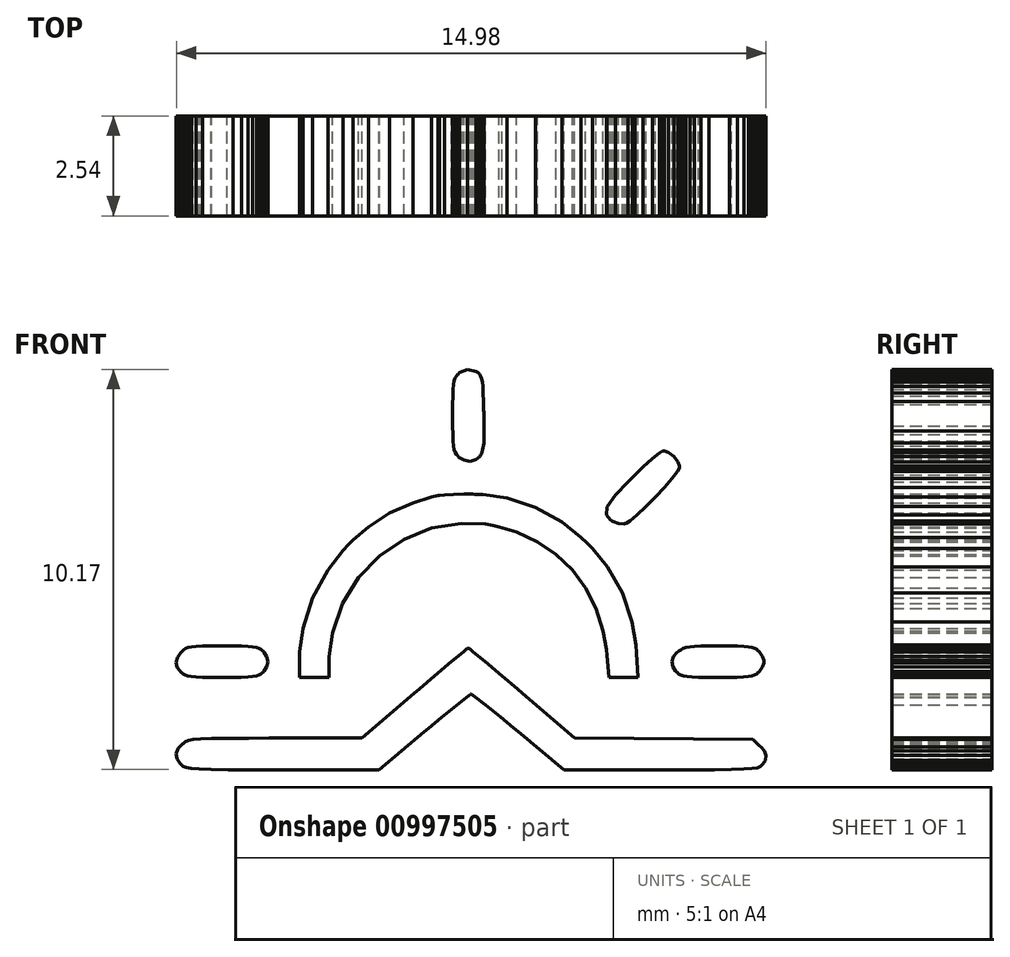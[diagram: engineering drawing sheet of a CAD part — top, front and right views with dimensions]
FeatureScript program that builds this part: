
annotation { "Feature Type Name" : "Feature", "Feature Type Description" : "" }
export const myFeature = defineFeature(function(context is Context, id is Id, definition is map)
    precondition{}
    {
        {
            var Q0;
            Q0=qCreatedBy(makeId("Front.planeOp"),FACE);
            var sketch = newSketch(context, id + "F0", { "sketchPlane" : qUnion([Q0])});
            skLineSegment(sketch, "E0", {"start": v(10.8, 42.86) * mm, "end": v(-8.25, 61.91) * mm});
            skLineSegment(sketch, "E1", {"start": v(-8.26, 61.91) * mm, "end": v(-10.8, 61.91) * mm});
            skLineSegment(sketch, "E2", {"start": v(-10.8, 61.91) * mm, "end": v(-10.8, -61.91) * mm});
            skLineSegment(sketch, "E3", {"start": v(-8.26, -61.91) * mm, "end": v(-10.8, -61.91) * mm});
            skLineSegment(sketch, "E4", {"start": v(-8.26, -61.91) * mm, "end": v(10.8, -42.86) * mm});
            skLineSegment(sketch, "E5", {"start": v(10.8, 42.86) * mm, "end": v(10.8, -42.86) * mm});
            skSolve(sketch);
        }
        {
            var Q0;
            Q0=makeQuery(id+"F0.imprint","IMPRINT",FACE,{"disambiguationData":[TD([[makeQuery(id+"F0.imprint","IMPRINT",EDGE,{"derivedFrom":sQuery(id+"F0.wireOp",EDGE,"E0")}),1.0]])]});
            var sketch = newSketch(context, id + "F1", { "sketchPlane" : qUnion([Q0])});
            skLineSegment(sketch, "E6", {"start": v(-0.33, 44.58) * mm, "end": v(-0.34, 44.57) * mm});
            skLineSegment(sketch, "E7", {"start": v(-0.34, 44.57) * mm, "end": v(-0.37, 44.54) * mm});
            skLineSegment(sketch, "E8", {"start": v(-0.37, 44.54) * mm, "end": v(-0.4, 44.49) * mm});
            skLineSegment(sketch, "E9", {"start": v(-0.4, 44.49) * mm, "end": v(-0.43, 44.42) * mm});
            skLineSegment(sketch, "E10", {"start": v(-0.43, 44.42) * mm, "end": v(-0.45, 44.33) * mm});
            skLineSegment(sketch, "E11", {"start": v(-0.45, 44.33) * mm, "end": v(-0.46, 44.2) * mm});
            skLineSegment(sketch, "E12", {"start": v(-0.46, 44.2) * mm, "end": v(-0.46, 44.04) * mm});
            skLineSegment(sketch, "E13", {"start": v(-0.46, 44.04) * mm, "end": v(-0.47, 43.82) * mm});
            skLineSegment(sketch, "E14", {"start": v(-0.47, 43.82) * mm, "end": v(-0.47, 43.61) * mm});
            skLineSegment(sketch, "E15", {"start": v(-0.47, 43.61) * mm, "end": v(-0.47, 43.55) * mm});
            skLineSegment(sketch, "E16", {"start": v(-0.47, 43.55) * mm, "end": v(-0.47, 43.48) * mm});
            skLineSegment(sketch, "E17", {"start": v(-0.47, 43.48) * mm, "end": v(-0.47, 43.27) * mm});
            skLineSegment(sketch, "E18", {"start": v(-0.47, 43.27) * mm, "end": v(-0.46, 43.06) * mm});
            skLineSegment(sketch, "E19", {"start": v(-0.46, 43.06) * mm, "end": v(-0.46, 42.89) * mm});
            skLineSegment(sketch, "E20", {"start": v(-0.46, 42.89) * mm, "end": v(-0.45, 42.77) * mm});
            skLineSegment(sketch, "E21", {"start": v(-0.45, 42.77) * mm, "end": v(-0.43, 42.67) * mm});
            skLineSegment(sketch, "E22", {"start": v(-0.43, 42.67) * mm, "end": v(-0.4, 42.6) * mm});
            skLineSegment(sketch, "E23", {"start": v(-0.4, 42.6) * mm, "end": v(-0.37, 42.55) * mm});
            skLineSegment(sketch, "E24", {"start": v(-0.37, 42.55) * mm, "end": v(-0.35, 42.52) * mm});
            skLineSegment(sketch, "E25", {"start": v(-0.35, 42.52) * mm, "end": v(-0.33, 42.5) * mm});
            skLineSegment(sketch, "E26", {"start": v(-0.33, 42.5) * mm, "end": v(-0.3, 42.48) * mm});
            skLineSegment(sketch, "E27", {"start": v(-0.3, 42.48) * mm, "end": v(-0.18, 42.4) * mm});
            skLineSegment(sketch, "E28", {"start": v(-0.18, 42.4) * mm, "end": v(-0.03, 42.37) * mm});
            skLineSegment(sketch, "E29", {"start": v(-0.03, 42.37) * mm, "end": v(0.12, 42.42) * mm});
            skLineSegment(sketch, "E30", {"start": v(0.12, 42.42) * mm, "end": v(0.22, 42.5) * mm});
            skLineSegment(sketch, "E31", {"start": v(0.22, 42.5) * mm, "end": v(0.24, 42.53) * mm});
            skLineSegment(sketch, "E32", {"start": v(0.24, 42.53) * mm, "end": v(0.26, 42.56) * mm});
            skLineSegment(sketch, "E33", {"start": v(0.26, 42.56) * mm, "end": v(0.3, 42.66) * mm});
            skLineSegment(sketch, "E34", {"start": v(0.3, 42.66) * mm, "end": v(0.32, 42.84) * mm});
            skLineSegment(sketch, "E35", {"start": v(0.32, 42.84) * mm, "end": v(0.33, 43.15) * mm});
            skLineSegment(sketch, "E36", {"start": v(0.33, 43.15) * mm, "end": v(0.33, 43.5) * mm});
            skLineSegment(sketch, "E37", {"start": v(0.33, 43.5) * mm, "end": v(0.32, 43.61) * mm});
            skLineSegment(sketch, "E38", {"start": v(0.32, 43.61) * mm, "end": v(0.32, 43.68) * mm});
            skLineSegment(sketch, "E39", {"start": v(0.32, 43.68) * mm, "end": v(0.31, 43.89) * mm});
            skLineSegment(sketch, "E40", {"start": v(0.31, 43.89) * mm, "end": v(0.3, 44.1) * mm});
            skLineSegment(sketch, "E41", {"start": v(0.3, 44.1) * mm, "end": v(0.3, 44.27) * mm});
            skLineSegment(sketch, "E42", {"start": v(0.3, 44.27) * mm, "end": v(0.28, 44.4) * mm});
            skLineSegment(sketch, "E43", {"start": v(0.28, 44.4) * mm, "end": v(0.27, 44.48) * mm});
            skLineSegment(sketch, "E44", {"start": v(0.27, 44.48) * mm, "end": v(0.24, 44.54) * mm});
            skLineSegment(sketch, "E45", {"start": v(0.24, 44.54) * mm, "end": v(0.21, 44.59) * mm});
            skLineSegment(sketch, "E46", {"start": v(0.21, 44.59) * mm, "end": v(0.18, 44.62) * mm});
            skLineSegment(sketch, "E47", {"start": v(0.18, 44.62) * mm, "end": v(0.17, 44.62) * mm});
            skLineSegment(sketch, "E48", {"start": v(0.17, 44.62) * mm, "end": v(0.13, 44.66) * mm});
            skLineSegment(sketch, "E49", {"start": v(0.13, 44.66) * mm, "end": v(-0.09, 44.71) * mm});
            skLineSegment(sketch, "E50", {"start": v(-0.09, 44.71) * mm, "end": v(-0.3, 44.62) * mm});
            skLineSegment(sketch, "E51", {"start": v(-0.3, 44.62) * mm, "end": v(-0.33, 44.58) * mm});
            skLineSegment(sketch, "E52", {"start": v(-5.3, 42.5) * mm, "end": v(-5.3, 42.49) * mm});
            skLineSegment(sketch, "E53", {"start": v(-5.3, 42.49) * mm, "end": v(-5.39, 42.37) * mm});
            skLineSegment(sketch, "E54", {"start": v(-5.39, 42.37) * mm, "end": v(-5.43, 42.26) * mm});
            skLineSegment(sketch, "E55", {"start": v(-5.43, 42.26) * mm, "end": v(-5.43, 42.23) * mm});
            skLineSegment(sketch, "E56", {"start": v(-5.43, 42.23) * mm, "end": v(-5.43, 42.2) * mm});
            skLineSegment(sketch, "E57", {"start": v(-5.43, 42.2) * mm, "end": v(-5.37, 42.1) * mm});
            skLineSegment(sketch, "E58", {"start": v(-5.37, 42.1) * mm, "end": v(-5.23, 41.91) * mm});
            skLineSegment(sketch, "E59", {"start": v(-5.23, 41.91) * mm, "end": v(-5.02, 41.68) * mm});
            skLineSegment(sketch, "E60", {"start": v(-5.02, 41.68) * mm, "end": v(-4.77, 41.42) * mm});
            skLineSegment(sketch, "E61", {"start": v(-4.77, 41.42) * mm, "end": v(-4.52, 41.17) * mm});
            skLineSegment(sketch, "E62", {"start": v(-4.52, 41.17) * mm, "end": v(-4.28, 40.97) * mm});
            skLineSegment(sketch, "E63", {"start": v(-4.28, 40.97) * mm, "end": v(-4.09, 40.82) * mm});
            skLineSegment(sketch, "E64", {"start": v(-4.09, 40.82) * mm, "end": v(-4, 40.77) * mm});
            skLineSegment(sketch, "E65", {"start": v(-4, 40.77) * mm, "end": v(-3.96, 40.77) * mm});
            skLineSegment(sketch, "E66", {"start": v(-3.96, 40.77) * mm, "end": v(-3.93, 40.77) * mm});
            skLineSegment(sketch, "E67", {"start": v(-3.93, 40.77) * mm, "end": v(-3.83, 40.8) * mm});
            skLineSegment(sketch, "E68", {"start": v(-3.83, 40.8) * mm, "end": v(-3.7, 40.9) * mm});
            skLineSegment(sketch, "E69", {"start": v(-3.7, 40.9) * mm, "end": v(-3.6, 41.02) * mm});
            skLineSegment(sketch, "E70", {"start": v(-3.6, 41.02) * mm, "end": v(-3.55, 41.1) * mm});
            skLineSegment(sketch, "E71", {"start": v(-3.55, 41.1) * mm, "end": v(-3.55, 41.14) * mm});
            skLineSegment(sketch, "E72", {"start": v(-3.55, 41.14) * mm, "end": v(-3.55, 41.17) * mm});
            skLineSegment(sketch, "E73", {"start": v(-3.55, 41.17) * mm, "end": v(-3.6, 41.25) * mm});
            skLineSegment(sketch, "E74", {"start": v(-3.6, 41.25) * mm, "end": v(-3.76, 41.44) * mm});
            skLineSegment(sketch, "E75", {"start": v(-3.76, 41.44) * mm, "end": v(-3.98, 41.68) * mm});
            skLineSegment(sketch, "E76", {"start": v(-3.98, 41.68) * mm, "end": v(-4.24, 41.95) * mm});
            skLineSegment(sketch, "E77", {"start": v(-4.24, 41.95) * mm, "end": v(-4.5, 42.2) * mm});
            skLineSegment(sketch, "E78", {"start": v(-4.5, 42.2) * mm, "end": v(-4.74, 42.43) * mm});
            skLineSegment(sketch, "E79", {"start": v(-4.74, 42.43) * mm, "end": v(-4.93, 42.58) * mm});
            skLineSegment(sketch, "E80", {"start": v(-4.93, 42.58) * mm, "end": v(-5, 42.64) * mm});
            skLineSegment(sketch, "E81", {"start": v(-5, 42.64) * mm, "end": v(-5.04, 42.64) * mm});
            skLineSegment(sketch, "E82", {"start": v(-5.04, 42.64) * mm, "end": v(-5.07, 42.64) * mm});
            skLineSegment(sketch, "E83", {"start": v(-5.07, 42.64) * mm, "end": v(-5.16, 42.6) * mm});
            skLineSegment(sketch, "E84", {"start": v(-5.16, 42.6) * mm, "end": v(-5.27, 42.53) * mm});
            skLineSegment(sketch, "E85", {"start": v(-5.27, 42.53) * mm, "end": v(-5.3, 42.5) * mm});
            skLineSegment(sketch, "E86", {"start": v(4.1, 41.96) * mm, "end": v(3.98, 41.85) * mm});
            skLineSegment(sketch, "E87", {"start": v(3.98, 41.85) * mm, "end": v(3.66, 41.51) * mm});
            skLineSegment(sketch, "E88", {"start": v(3.66, 41.51) * mm, "end": v(3.45, 41.21) * mm});
            skLineSegment(sketch, "E89", {"start": v(3.45, 41.21) * mm, "end": v(3.43, 41.01) * mm});
            skLineSegment(sketch, "E90", {"start": v(3.43, 41.01) * mm, "end": v(3.54, 40.89) * mm});
            skLineSegment(sketch, "E91", {"start": v(3.54, 40.89) * mm, "end": v(3.58, 40.86) * mm});
            skLineSegment(sketch, "E92", {"start": v(3.58, 40.86) * mm, "end": v(3.6, 40.84) * mm});
            skLineSegment(sketch, "E93", {"start": v(3.6, 40.84) * mm, "end": v(3.74, 40.8) * mm});
            skLineSegment(sketch, "E94", {"start": v(3.74, 40.8) * mm, "end": v(3.88, 40.79) * mm});
            skLineSegment(sketch, "E95", {"start": v(3.88, 40.79) * mm, "end": v(3.9, 40.8) * mm});
            skLineSegment(sketch, "E96", {"start": v(3.9, 40.8) * mm, "end": v(3.94, 40.8) * mm});
            skLineSegment(sketch, "E97", {"start": v(3.94, 40.8) * mm, "end": v(4.03, 40.86) * mm});
            skLineSegment(sketch, "E98", {"start": v(4.03, 40.86) * mm, "end": v(4.22, 41.01) * mm});
            skLineSegment(sketch, "E99", {"start": v(4.22, 41.01) * mm, "end": v(4.44, 41.22) * mm});
            skLineSegment(sketch, "E100", {"start": v(4.44, 41.22) * mm, "end": v(4.68, 41.46) * mm});
            skLineSegment(sketch, "E101", {"start": v(4.68, 41.46) * mm, "end": v(4.91, 41.7) * mm});
            skLineSegment(sketch, "E102", {"start": v(4.91, 41.7) * mm, "end": v(5.1, 41.94) * mm});
            skLineSegment(sketch, "E103", {"start": v(5.1, 41.94) * mm, "end": v(5.24, 42.12) * mm});
            skLineSegment(sketch, "E104", {"start": v(5.24, 42.12) * mm, "end": v(5.3, 42.2) * mm});
            skLineSegment(sketch, "E105", {"start": v(5.3, 42.2) * mm, "end": v(5.3, 42.23) * mm});
            skLineSegment(sketch, "E106", {"start": v(5.3, 42.23) * mm, "end": v(5.3, 42.26) * mm});
            skLineSegment(sketch, "E107", {"start": v(5.3, 42.26) * mm, "end": v(5.25, 42.36) * mm});
            skLineSegment(sketch, "E108", {"start": v(5.25, 42.36) * mm, "end": v(5.15, 42.5) * mm});
            skLineSegment(sketch, "E109", {"start": v(5.15, 42.5) * mm, "end": v(5.02, 42.6) * mm});
            skLineSegment(sketch, "E110", {"start": v(5.02, 42.6) * mm, "end": v(4.92, 42.64) * mm});
            skLineSegment(sketch, "E111", {"start": v(4.92, 42.64) * mm, "end": v(4.88, 42.64) * mm});
            skLineSegment(sketch, "E112", {"start": v(4.88, 42.64) * mm, "end": v(4.86, 42.64) * mm});
            skLineSegment(sketch, "E113", {"start": v(4.86, 42.64) * mm, "end": v(4.78, 42.59) * mm});
            skLineSegment(sketch, "E114", {"start": v(4.78, 42.59) * mm, "end": v(4.6, 42.44) * mm});
            skLineSegment(sketch, "E115", {"start": v(4.6, 42.44) * mm, "end": v(4.36, 42.23) * mm});
            skLineSegment(sketch, "E116", {"start": v(4.36, 42.23) * mm, "end": v(4.16, 42.03) * mm});
            skLineSegment(sketch, "E117", {"start": v(4.16, 42.03) * mm, "end": v(4.1, 41.96) * mm});
            skLineSegment(sketch, "E118", {"start": v(-0.84, 41.5) * mm, "end": v(-1, 41.47) * mm});
            skLineSegment(sketch, "E119", {"start": v(-1, 41.47) * mm, "end": v(-1.48, 41.32) * mm});
            skLineSegment(sketch, "E120", {"start": v(-1.48, 41.32) * mm, "end": v(-2.07, 41.06) * mm});
            skLineSegment(sketch, "E121", {"start": v(-2.07, 41.06) * mm, "end": v(-2.6, 40.7) * mm});
            skLineSegment(sketch, "E122", {"start": v(-2.6, 40.7) * mm, "end": v(-3, 40.38) * mm});
            skLineSegment(sketch, "E123", {"start": v(-3, 40.38) * mm, "end": v(-3.11, 40.26) * mm});
            skLineSegment(sketch, "E124", {"start": v(-3.11, 40.26) * mm, "end": v(-3.26, 40.11) * mm});
            skLineSegment(sketch, "E125", {"start": v(-3.26, 40.11) * mm, "end": v(-3.64, 39.62) * mm});
            skLineSegment(sketch, "E126", {"start": v(-3.64, 39.62) * mm, "end": v(-4.03, 38.9) * mm});
            skLineSegment(sketch, "E127", {"start": v(-4.03, 38.9) * mm, "end": v(-4.27, 38.13) * mm});
            skLineSegment(sketch, "E128", {"start": v(-4.27, 38.13) * mm, "end": v(-4.35, 37.53) * mm});
            skLineSegment(sketch, "E129", {"start": v(-4.35, 37.53) * mm, "end": v(-4.35, 37.34) * mm});
            skLineSegment(sketch, "E130", {"start": v(-4.35, 37.34) * mm, "end": v(-4.35, 36.88) * mm});
            skLineSegment(sketch, "E131", {"start": v(-4.35, 36.88) * mm, "end": v(-3.62, 36.88) * mm});
            skLineSegment(sketch, "E132", {"start": v(-3.62, 36.88) * mm, "end": v(-3.62, 37.2) * mm});
            skLineSegment(sketch, "E133", {"start": v(-3.62, 37.2) * mm, "end": v(-3.62, 37.4) * mm});
            skLineSegment(sketch, "E134", {"start": v(-3.62, 37.4) * mm, "end": v(-3.52, 38.02) * mm});
            skLineSegment(sketch, "E135", {"start": v(-3.52, 38.02) * mm, "end": v(-3.26, 38.76) * mm});
            skLineSegment(sketch, "E136", {"start": v(-3.26, 38.76) * mm, "end": v(-2.86, 39.42) * mm});
            skLineSegment(sketch, "E137", {"start": v(-2.86, 39.42) * mm, "end": v(-2.33, 39.97) * mm});
            skLineSegment(sketch, "E138", {"start": v(-2.33, 39.97) * mm, "end": v(-1.7, 40.4) * mm});
            skLineSegment(sketch, "E139", {"start": v(-1.7, 40.4) * mm, "end": v(-1, 40.68) * mm});
            skLineSegment(sketch, "E140", {"start": v(-1, 40.68) * mm, "end": v(-0.24, 40.8) * mm});
            skLineSegment(sketch, "E141", {"start": v(-0.24, 40.8) * mm, "end": v(0.36, 40.78) * mm});
            skLineSegment(sketch, "E142", {"start": v(0.36, 40.78) * mm, "end": v(0.56, 40.74) * mm});
            skLineSegment(sketch, "E143", {"start": v(0.56, 40.74) * mm, "end": v(0.7, 40.7) * mm});
            skLineSegment(sketch, "E144", {"start": v(0.7, 40.7) * mm, "end": v(1.15, 40.58) * mm});
            skLineSegment(sketch, "E145", {"start": v(1.15, 40.58) * mm, "end": v(1.68, 40.33) * mm});
            skLineSegment(sketch, "E146", {"start": v(1.68, 40.33) * mm, "end": v(2.16, 40) * mm});
            skLineSegment(sketch, "E147", {"start": v(2.16, 40) * mm, "end": v(2.57, 39.61) * mm});
            skLineSegment(sketch, "E148", {"start": v(2.57, 39.61) * mm, "end": v(2.9, 39.15) * mm});
            skLineSegment(sketch, "E149", {"start": v(2.9, 39.15) * mm, "end": v(3.17, 38.63) * mm});
            skLineSegment(sketch, "E150", {"start": v(3.17, 38.63) * mm, "end": v(3.35, 38.06) * mm});
            skLineSegment(sketch, "E151", {"start": v(3.35, 38.06) * mm, "end": v(3.44, 37.6) * mm});
            skLineSegment(sketch, "E152", {"start": v(3.44, 37.6) * mm, "end": v(3.45, 37.44) * mm});
            skLineSegment(sketch, "E153", {"start": v(3.45, 37.44) * mm, "end": v(3.5, 36.88) * mm});
            skLineSegment(sketch, "E154", {"start": v(3.5, 36.88) * mm, "end": v(4.24, 36.88) * mm});
            skLineSegment(sketch, "E155", {"start": v(4.24, 36.88) * mm, "end": v(4.2, 37.5) * mm});
            skLineSegment(sketch, "E156", {"start": v(4.2, 37.5) * mm, "end": v(4.19, 37.7) * mm});
            skLineSegment(sketch, "E157", {"start": v(4.19, 37.7) * mm, "end": v(4.09, 38.3) * mm});
            skLineSegment(sketch, "E158", {"start": v(4.09, 38.3) * mm, "end": v(3.84, 39.02) * mm});
            skLineSegment(sketch, "E159", {"start": v(3.84, 39.02) * mm, "end": v(3.46, 39.69) * mm});
            skLineSegment(sketch, "E160", {"start": v(3.46, 39.69) * mm, "end": v(3.08, 40.16) * mm});
            skLineSegment(sketch, "E161", {"start": v(3.08, 40.16) * mm, "end": v(2.94, 40.3) * mm});
            skLineSegment(sketch, "E162", {"start": v(2.94, 40.3) * mm, "end": v(2.8, 40.44) * mm});
            skLineSegment(sketch, "E163", {"start": v(2.8, 40.44) * mm, "end": v(2.3, 40.83) * mm});
            skLineSegment(sketch, "E164", {"start": v(2.3, 40.83) * mm, "end": v(1.64, 41.2) * mm});
            skLineSegment(sketch, "E165", {"start": v(1.64, 41.2) * mm, "end": v(0.9, 41.44) * mm});
            skLineSegment(sketch, "E166", {"start": v(0.9, 41.44) * mm, "end": v(0.3, 41.53) * mm});
            skLineSegment(sketch, "E167", {"start": v(0.3, 41.53) * mm, "end": v(0.1, 41.54) * mm});
            skLineSegment(sketch, "E168", {"start": v(0.1, 41.54) * mm, "end": v(0.03, 41.54) * mm});
            skLineSegment(sketch, "E169", {"start": v(0.03, 41.54) * mm, "end": v(-0.18, 41.54) * mm});
            skLineSegment(sketch, "E170", {"start": v(-0.18, 41.54) * mm, "end": v(-0.45, 41.54) * mm});
            skLineSegment(sketch, "E171", {"start": v(-0.45, 41.54) * mm, "end": v(-0.68, 41.52) * mm});
            skLineSegment(sketch, "E172", {"start": v(-0.68, 41.52) * mm, "end": v(-0.8, 41.51) * mm});
            skLineSegment(sketch, "E173", {"start": v(-0.8, 41.51) * mm, "end": v(-0.84, 41.5) * mm});
            skLineSegment(sketch, "E174", {"start": v(-7.35, 37.53) * mm, "end": v(-7.38, 37.5) * mm});
            skLineSegment(sketch, "E175", {"start": v(-7.38, 37.5) * mm, "end": v(-7.46, 37.4) * mm});
            skLineSegment(sketch, "E176", {"start": v(-7.46, 37.4) * mm, "end": v(-7.5, 37.26) * mm});
            skLineSegment(sketch, "E177", {"start": v(-7.5, 37.26) * mm, "end": v(-7.46, 37.14) * mm});
            skLineSegment(sketch, "E178", {"start": v(-7.46, 37.14) * mm, "end": v(-7.4, 37.04) * mm});
            skLineSegment(sketch, "E179", {"start": v(-7.4, 37.04) * mm, "end": v(-7.37, 37.01) * mm});
            skLineSegment(sketch, "E180", {"start": v(-7.37, 37.01) * mm, "end": v(-7.36, 37) * mm});
            skLineSegment(sketch, "E181", {"start": v(-7.36, 37) * mm, "end": v(-7.32, 36.97) * mm});
            skLineSegment(sketch, "E182", {"start": v(-7.32, 36.97) * mm, "end": v(-7.27, 36.94) * mm});
            skLineSegment(sketch, "E183", {"start": v(-7.27, 36.94) * mm, "end": v(-7.2, 36.92) * mm});
            skLineSegment(sketch, "E184", {"start": v(-7.2, 36.92) * mm, "end": v(-7.1, 36.9) * mm});
            skLineSegment(sketch, "E185", {"start": v(-7.1, 36.9) * mm, "end": v(-6.99, 36.9) * mm});
            skLineSegment(sketch, "E186", {"start": v(-6.99, 36.9) * mm, "end": v(-6.82, 36.88) * mm});
            skLineSegment(sketch, "E187", {"start": v(-6.82, 36.88) * mm, "end": v(-6.6, 36.88) * mm});
            skLineSegment(sketch, "E188", {"start": v(-6.6, 36.88) * mm, "end": v(-6.4, 36.88) * mm});
            skLineSegment(sketch, "E189", {"start": v(-6.4, 36.88) * mm, "end": v(-6.33, 36.88) * mm});
            skLineSegment(sketch, "E190", {"start": v(-6.33, 36.88) * mm, "end": v(-6.26, 36.88) * mm});
            skLineSegment(sketch, "E191", {"start": v(-6.26, 36.88) * mm, "end": v(-6.06, 36.88) * mm});
            skLineSegment(sketch, "E192", {"start": v(-6.06, 36.88) * mm, "end": v(-5.84, 36.88) * mm});
            skLineSegment(sketch, "E193", {"start": v(-5.84, 36.88) * mm, "end": v(-5.67, 36.9) * mm});
            skLineSegment(sketch, "E194", {"start": v(-5.67, 36.9) * mm, "end": v(-5.55, 36.9) * mm});
            skLineSegment(sketch, "E195", {"start": v(-5.55, 36.9) * mm, "end": v(-5.46, 36.92) * mm});
            skLineSegment(sketch, "E196", {"start": v(-5.46, 36.92) * mm, "end": v(-5.39, 36.94) * mm});
            skLineSegment(sketch, "E197", {"start": v(-5.39, 36.94) * mm, "end": v(-5.34, 36.97) * mm});
            skLineSegment(sketch, "E198", {"start": v(-5.34, 36.97) * mm, "end": v(-5.3, 37) * mm});
            skLineSegment(sketch, "E199", {"start": v(-5.3, 37) * mm, "end": v(-5.3, 37.01) * mm});
            skLineSegment(sketch, "E200", {"start": v(-5.3, 37.01) * mm, "end": v(-5.26, 37.04) * mm});
            skLineSegment(sketch, "E201", {"start": v(-5.26, 37.04) * mm, "end": v(-5.2, 37.15) * mm});
            skLineSegment(sketch, "E202", {"start": v(-5.2, 37.15) * mm, "end": v(-5.17, 37.28) * mm});
            skLineSegment(sketch, "E203", {"start": v(-5.17, 37.28) * mm, "end": v(-5.2, 37.42) * mm});
            skLineSegment(sketch, "E204", {"start": v(-5.2, 37.42) * mm, "end": v(-5.26, 37.52) * mm});
            skLineSegment(sketch, "E205", {"start": v(-5.26, 37.52) * mm, "end": v(-5.3, 37.55) * mm});
            skLineSegment(sketch, "E206", {"start": v(-5.3, 37.55) * mm, "end": v(-5.3, 37.56) * mm});
            skLineSegment(sketch, "E207", {"start": v(-5.3, 37.56) * mm, "end": v(-5.34, 37.6) * mm});
            skLineSegment(sketch, "E208", {"start": v(-5.34, 37.6) * mm, "end": v(-5.39, 37.62) * mm});
            skLineSegment(sketch, "E209", {"start": v(-5.39, 37.62) * mm, "end": v(-5.46, 37.65) * mm});
            skLineSegment(sketch, "E210", {"start": v(-5.46, 37.65) * mm, "end": v(-5.55, 37.66) * mm});
            skLineSegment(sketch, "E211", {"start": v(-5.55, 37.66) * mm, "end": v(-5.67, 37.67) * mm});
            skLineSegment(sketch, "E212", {"start": v(-5.67, 37.67) * mm, "end": v(-5.83, 37.68) * mm});
            skLineSegment(sketch, "E213", {"start": v(-5.83, 37.68) * mm, "end": v(-6.05, 37.68) * mm});
            skLineSegment(sketch, "E214", {"start": v(-6.05, 37.68) * mm, "end": v(-6.25, 37.68) * mm});
            skLineSegment(sketch, "E215", {"start": v(-6.25, 37.68) * mm, "end": v(-6.32, 37.68) * mm});
            skLineSegment(sketch, "E216", {"start": v(-6.32, 37.68) * mm, "end": v(-6.39, 37.68) * mm});
            skLineSegment(sketch, "E217", {"start": v(-6.39, 37.68) * mm, "end": v(-6.6, 37.68) * mm});
            skLineSegment(sketch, "E218", {"start": v(-6.6, 37.68) * mm, "end": v(-6.82, 37.68) * mm});
            skLineSegment(sketch, "E219", {"start": v(-6.82, 37.68) * mm, "end": v(-6.98, 37.67) * mm});
            skLineSegment(sketch, "E220", {"start": v(-6.98, 37.67) * mm, "end": v(-7.1, 37.66) * mm});
            skLineSegment(sketch, "E221", {"start": v(-7.1, 37.66) * mm, "end": v(-7.2, 37.64) * mm});
            skLineSegment(sketch, "E222", {"start": v(-7.2, 37.64) * mm, "end": v(-7.26, 37.62) * mm});
            skLineSegment(sketch, "E223", {"start": v(-7.26, 37.62) * mm, "end": v(-7.3, 37.58) * mm});
            skLineSegment(sketch, "E224", {"start": v(-7.3, 37.58) * mm, "end": v(-7.34, 37.54) * mm});
            skLineSegment(sketch, "E225", {"start": v(-7.34, 37.54) * mm, "end": v(-7.35, 37.53) * mm});
            skLineSegment(sketch, "E226", {"start": v(5.27, 37.54) * mm, "end": v(5.23, 37.52) * mm});
            skLineSegment(sketch, "E227", {"start": v(5.23, 37.52) * mm, "end": v(5.15, 37.42) * mm});
            skLineSegment(sketch, "E228", {"start": v(5.15, 37.42) * mm, "end": v(5.1, 37.29) * mm});
            skLineSegment(sketch, "E229", {"start": v(5.1, 37.29) * mm, "end": v(5.13, 37.15) * mm});
            skLineSegment(sketch, "E230", {"start": v(5.13, 37.15) * mm, "end": v(5.2, 37.04) * mm});
            skLineSegment(sketch, "E231", {"start": v(5.2, 37.04) * mm, "end": v(5.23, 37.01) * mm});
            skLineSegment(sketch, "E232", {"start": v(5.23, 37.01) * mm, "end": v(5.24, 37) * mm});
            skLineSegment(sketch, "E233", {"start": v(5.24, 37) * mm, "end": v(5.27, 36.97) * mm});
            skLineSegment(sketch, "E234", {"start": v(5.27, 36.97) * mm, "end": v(5.32, 36.94) * mm});
            skLineSegment(sketch, "E235", {"start": v(5.32, 36.94) * mm, "end": v(5.4, 36.92) * mm});
            skLineSegment(sketch, "E236", {"start": v(5.4, 36.92) * mm, "end": v(5.48, 36.9) * mm});
            skLineSegment(sketch, "E237", {"start": v(5.48, 36.9) * mm, "end": v(5.6, 36.9) * mm});
            skLineSegment(sketch, "E238", {"start": v(5.6, 36.9) * mm, "end": v(5.77, 36.88) * mm});
            skLineSegment(sketch, "E239", {"start": v(5.77, 36.88) * mm, "end": v(5.99, 36.88) * mm});
            skLineSegment(sketch, "E240", {"start": v(5.99, 36.88) * mm, "end": v(6.2, 36.88) * mm});
            skLineSegment(sketch, "E241", {"start": v(6.2, 36.88) * mm, "end": v(6.26, 36.88) * mm});
            skLineSegment(sketch, "E242", {"start": v(6.26, 36.88) * mm, "end": v(6.33, 36.88) * mm});
            skLineSegment(sketch, "E243", {"start": v(6.33, 36.88) * mm, "end": v(6.54, 36.88) * mm});
            skLineSegment(sketch, "E244", {"start": v(6.54, 36.88) * mm, "end": v(6.75, 36.88) * mm});
            skLineSegment(sketch, "E245", {"start": v(6.75, 36.88) * mm, "end": v(6.92, 36.9) * mm});
            skLineSegment(sketch, "E246", {"start": v(6.92, 36.9) * mm, "end": v(7.04, 36.9) * mm});
            skLineSegment(sketch, "E247", {"start": v(7.04, 36.9) * mm, "end": v(7.14, 36.92) * mm});
            skLineSegment(sketch, "E248", {"start": v(7.14, 36.92) * mm, "end": v(7.2, 36.94) * mm});
            skLineSegment(sketch, "E249", {"start": v(7.2, 36.94) * mm, "end": v(7.26, 36.97) * mm});
            skLineSegment(sketch, "E250", {"start": v(7.26, 36.97) * mm, "end": v(7.3, 37) * mm});
            skLineSegment(sketch, "E251", {"start": v(7.3, 37) * mm, "end": v(7.3, 37.01) * mm});
            skLineSegment(sketch, "E252", {"start": v(7.3, 37.01) * mm, "end": v(7.32, 37.03) * mm});
            skLineSegment(sketch, "E253", {"start": v(7.32, 37.03) * mm, "end": v(7.4, 37.15) * mm});
            skLineSegment(sketch, "E254", {"start": v(7.4, 37.15) * mm, "end": v(7.44, 37.25) * mm});
            skLineSegment(sketch, "E255", {"start": v(7.44, 37.25) * mm, "end": v(7.44, 37.28) * mm});
            skLineSegment(sketch, "E256", {"start": v(7.44, 37.28) * mm, "end": v(7.44, 37.32) * mm});
            skLineSegment(sketch, "E257", {"start": v(7.44, 37.32) * mm, "end": v(7.4, 37.42) * mm});
            skLineSegment(sketch, "E258", {"start": v(7.4, 37.42) * mm, "end": v(7.32, 37.53) * mm});
            skLineSegment(sketch, "E259", {"start": v(7.32, 37.53) * mm, "end": v(7.3, 37.55) * mm});
            skLineSegment(sketch, "E260", {"start": v(7.3, 37.55) * mm, "end": v(7.3, 37.56) * mm});
            skLineSegment(sketch, "E261", {"start": v(7.3, 37.56) * mm, "end": v(7.26, 37.6) * mm});
            skLineSegment(sketch, "E262", {"start": v(7.26, 37.6) * mm, "end": v(7.2, 37.62) * mm});
            skLineSegment(sketch, "E263", {"start": v(7.2, 37.62) * mm, "end": v(7.14, 37.65) * mm});
            skLineSegment(sketch, "E264", {"start": v(7.14, 37.65) * mm, "end": v(7.05, 37.66) * mm});
            skLineSegment(sketch, "E265", {"start": v(7.05, 37.66) * mm, "end": v(6.93, 37.67) * mm});
            skLineSegment(sketch, "E266", {"start": v(6.93, 37.67) * mm, "end": v(6.77, 37.68) * mm});
            skLineSegment(sketch, "E267", {"start": v(6.77, 37.68) * mm, "end": v(6.56, 37.68) * mm});
            skLineSegment(sketch, "E268", {"start": v(6.56, 37.68) * mm, "end": v(6.37, 37.68) * mm});
            skLineSegment(sketch, "E269", {"start": v(6.37, 37.68) * mm, "end": v(6.3, 37.68) * mm});
            skLineSegment(sketch, "E270", {"start": v(6.3, 37.68) * mm, "end": v(6.24, 37.68) * mm});
            skLineSegment(sketch, "E271", {"start": v(6.24, 37.68) * mm, "end": v(6.04, 37.68) * mm});
            skLineSegment(sketch, "E272", {"start": v(6.04, 37.68) * mm, "end": v(5.84, 37.68) * mm});
            skLineSegment(sketch, "E273", {"start": v(5.84, 37.68) * mm, "end": v(5.68, 37.67) * mm});
            skLineSegment(sketch, "E274", {"start": v(5.68, 37.67) * mm, "end": v(5.56, 37.66) * mm});
            skLineSegment(sketch, "E275", {"start": v(5.56, 37.66) * mm, "end": v(5.46, 37.64) * mm});
            skLineSegment(sketch, "E276", {"start": v(5.46, 37.64) * mm, "end": v(5.39, 37.62) * mm});
            skLineSegment(sketch, "E277", {"start": v(5.39, 37.62) * mm, "end": v(5.32, 37.59) * mm});
            skLineSegment(sketch, "E278", {"start": v(5.32, 37.59) * mm, "end": v(5.28, 37.55) * mm});
            skLineSegment(sketch, "E279", {"start": v(5.28, 37.55) * mm, "end": v(5.27, 37.54) * mm});
            skLineSegment(sketch, "E280", {"start": v(-1.45, 36.48) * mm, "end": v(-2.77, 35.34) * mm});
            skLineSegment(sketch, "E281", {"start": v(-2.77, 35.34) * mm, "end": v(-4.96, 35.34) * mm});
            skLineSegment(sketch, "E282", {"start": v(-4.96, 35.34) * mm, "end": v(-5.13, 35.34) * mm});
            skLineSegment(sketch, "E283", {"start": v(-5.13, 35.34) * mm, "end": v(-5.66, 35.34) * mm});
            skLineSegment(sketch, "E284", {"start": v(-5.66, 35.34) * mm, "end": v(-6.2, 35.34) * mm});
            skLineSegment(sketch, "E285", {"start": v(-6.2, 35.34) * mm, "end": v(-6.6, 35.33) * mm});
            skLineSegment(sketch, "E286", {"start": v(-6.6, 35.33) * mm, "end": v(-6.87, 35.32) * mm});
            skLineSegment(sketch, "E287", {"start": v(-6.87, 35.32) * mm, "end": v(-7.06, 35.3) * mm});
            skLineSegment(sketch, "E288", {"start": v(-7.06, 35.3) * mm, "end": v(-7.18, 35.28) * mm});
            skLineSegment(sketch, "E289", {"start": v(-7.18, 35.28) * mm, "end": v(-7.26, 35.24) * mm});
            skLineSegment(sketch, "E290", {"start": v(-7.26, 35.24) * mm, "end": v(-7.31, 35.21) * mm});
            skLineSegment(sketch, "E291", {"start": v(-7.31, 35.21) * mm, "end": v(-7.33, 35.2) * mm});
            skLineSegment(sketch, "E292", {"start": v(-7.33, 35.2) * mm, "end": v(-7.36, 35.17) * mm});
            skLineSegment(sketch, "E293", {"start": v(-7.36, 35.17) * mm, "end": v(-7.45, 35.07) * mm});
            skLineSegment(sketch, "E294", {"start": v(-7.45, 35.07) * mm, "end": v(-7.5, 34.94) * mm});
            skLineSegment(sketch, "E295", {"start": v(-7.5, 34.94) * mm, "end": v(-7.47, 34.8) * mm});
            skLineSegment(sketch, "E296", {"start": v(-7.47, 34.8) * mm, "end": v(-7.4, 34.7) * mm});
            skLineSegment(sketch, "E297", {"start": v(-7.4, 34.7) * mm, "end": v(-7.37, 34.67) * mm});
            skLineSegment(sketch, "E298", {"start": v(-7.37, 34.67) * mm, "end": v(-7.36, 34.66) * mm});
            skLineSegment(sketch, "E299", {"start": v(-7.36, 34.66) * mm, "end": v(-7.32, 34.63) * mm});
            skLineSegment(sketch, "E300", {"start": v(-7.32, 34.63) * mm, "end": v(-7.24, 34.6) * mm});
            skLineSegment(sketch, "E301", {"start": v(-7.24, 34.6) * mm, "end": v(-7.12, 34.57) * mm});
            skLineSegment(sketch, "E302", {"start": v(-7.12, 34.57) * mm, "end": v(-6.91, 34.56) * mm});
            skLineSegment(sketch, "E303", {"start": v(-6.91, 34.56) * mm, "end": v(-6.6, 34.54) * mm});
            skLineSegment(sketch, "E304", {"start": v(-6.6, 34.54) * mm, "end": v(-6.17, 34.54) * mm});
            skLineSegment(sketch, "E305", {"start": v(-6.17, 34.54) * mm, "end": v(-5.57, 34.54) * mm});
            skLineSegment(sketch, "E306", {"start": v(-5.57, 34.54) * mm, "end": v(-4.98, 34.54) * mm});
            skLineSegment(sketch, "E307", {"start": v(-4.98, 34.54) * mm, "end": v(-4.79, 34.54) * mm});
            skLineSegment(sketch, "E308", {"start": v(-4.79, 34.54) * mm, "end": v(-2.34, 34.54) * mm});
            skLineSegment(sketch, "E309", {"start": v(-2.34, 34.54) * mm, "end": v(-1.2, 35.5) * mm});
            skLineSegment(sketch, "E310", {"start": v(-1.2, 35.5) * mm, "end": v(-1.09, 35.59) * mm});
            skLineSegment(sketch, "E311", {"start": v(-1.09, 35.59) * mm, "end": v(-0.75, 35.86) * mm});
            skLineSegment(sketch, "E312", {"start": v(-0.75, 35.86) * mm, "end": v(-0.38, 36.17) * mm});
            skLineSegment(sketch, "E313", {"start": v(-0.38, 36.17) * mm, "end": v(-0.12, 36.38) * mm});
            skLineSegment(sketch, "E314", {"start": v(-0.12, 36.38) * mm, "end": v(-0.02, 36.46) * mm});
            skLineSegment(sketch, "E315", {"start": v(-0.02, 36.46) * mm, "end": v(-0.01, 36.46) * mm});
            skLineSegment(sketch, "E316", {"start": v(-0.01, 36.46) * mm, "end": v(0, 36.46) * mm});
            skLineSegment(sketch, "E317", {"start": v(0, 36.46) * mm, "end": v(0.1, 36.39) * mm});
            skLineSegment(sketch, "E318", {"start": v(0.1, 36.39) * mm, "end": v(0.36, 36.19) * mm});
            skLineSegment(sketch, "E319", {"start": v(0.36, 36.19) * mm, "end": v(0.74, 35.88) * mm});
            skLineSegment(sketch, "E320", {"start": v(0.74, 35.88) * mm, "end": v(1.08, 35.6) * mm});
            skLineSegment(sketch, "E321", {"start": v(1.08, 35.6) * mm, "end": v(1.2, 35.5) * mm});
            skLineSegment(sketch, "E322", {"start": v(1.2, 35.5) * mm, "end": v(2.36, 34.54) * mm});
            skLineSegment(sketch, "E323", {"start": v(2.36, 34.54) * mm, "end": v(4.82, 34.54) * mm});
            skLineSegment(sketch, "E324", {"start": v(4.82, 34.54) * mm, "end": v(5, 34.54) * mm});
            skLineSegment(sketch, "E325", {"start": v(5, 34.54) * mm, "end": v(5.58, 34.54) * mm});
            skLineSegment(sketch, "E326", {"start": v(5.58, 34.54) * mm, "end": v(6.18, 34.54) * mm});
            skLineSegment(sketch, "E327", {"start": v(6.18, 34.54) * mm, "end": v(6.62, 34.54) * mm});
            skLineSegment(sketch, "E328", {"start": v(6.62, 34.54) * mm, "end": v(6.93, 34.55) * mm});
            skLineSegment(sketch, "E329", {"start": v(6.93, 34.55) * mm, "end": v(7.14, 34.57) * mm});
            skLineSegment(sketch, "E330", {"start": v(7.14, 34.57) * mm, "end": v(7.27, 34.59) * mm});
            skLineSegment(sketch, "E331", {"start": v(7.27, 34.59) * mm, "end": v(7.34, 34.62) * mm});
            skLineSegment(sketch, "E332", {"start": v(7.34, 34.62) * mm, "end": v(7.38, 34.65) * mm});
            skLineSegment(sketch, "E333", {"start": v(7.38, 34.65) * mm, "end": v(7.39, 34.66) * mm});
            skLineSegment(sketch, "E334", {"start": v(7.39, 34.66) * mm, "end": v(7.41, 34.68) * mm});
            skLineSegment(sketch, "E335", {"start": v(7.41, 34.68) * mm, "end": v(7.48, 34.78) * mm});
            skLineSegment(sketch, "E336", {"start": v(7.48, 34.78) * mm, "end": v(7.5, 34.9) * mm});
            skLineSegment(sketch, "E337", {"start": v(7.5, 34.9) * mm, "end": v(7.45, 35.01) * mm});
            skLineSegment(sketch, "E338", {"start": v(7.45, 35.01) * mm, "end": v(7.36, 35.12) * mm});
            skLineSegment(sketch, "E339", {"start": v(7.36, 35.12) * mm, "end": v(7.33, 35.15) * mm});
            skLineSegment(sketch, "E340", {"start": v(7.33, 35.15) * mm, "end": v(7.15, 35.3) * mm});
            skLineSegment(sketch, "E341", {"start": v(7.15, 35.3) * mm, "end": v(2.63, 35.35) * mm});
            skLineSegment(sketch, "E342", {"start": v(2.63, 35.35) * mm, "end": v(1.3, 36.48) * mm});
            skLineSegment(sketch, "E343", {"start": v(1.3, 36.48) * mm, "end": v(1.17, 36.6) * mm});
            skLineSegment(sketch, "E344", {"start": v(1.17, 36.6) * mm, "end": v(0.78, 36.92) * mm});
            skLineSegment(sketch, "E345", {"start": v(0.78, 36.92) * mm, "end": v(0.35, 37.28) * mm});
            skLineSegment(sketch, "E346", {"start": v(0.35, 37.28) * mm, "end": v(0.05, 37.53) * mm});
            skLineSegment(sketch, "E347", {"start": v(0.05, 37.53) * mm, "end": v(-0.04, 37.62) * mm});
            skLineSegment(sketch, "E348", {"start": v(-0.04, 37.62) * mm, "end": v(-0.07, 37.62) * mm});
            skLineSegment(sketch, "E349", {"start": v(-0.07, 37.62) * mm, "end": v(-0.1, 37.62) * mm});
            skLineSegment(sketch, "E350", {"start": v(-0.1, 37.62) * mm, "end": v(-0.2, 37.53) * mm});
            skLineSegment(sketch, "E351", {"start": v(-0.2, 37.53) * mm, "end": v(-0.5, 37.28) * mm});
            skLineSegment(sketch, "E352", {"start": v(-0.5, 37.28) * mm, "end": v(-0.93, 36.92) * mm});
            skLineSegment(sketch, "E353", {"start": v(-0.93, 36.92) * mm, "end": v(-1.32, 36.6) * mm});
            skLineSegment(sketch, "E354", {"start": v(-1.32, 36.6) * mm, "end": v(-1.45, 36.48) * mm});
            skSolve(sketch);
        }
        {
            var Q0;
            Q0=makeQuery(id+"F1.imprint","IMPRINT",FACE,{"disambiguationData":[TD([[makeQuery(id+"F1.imprint","IMPRINT",EDGE,{"derivedFrom":sQuery(id+"F1.wireOp",EDGE,"E280")}),1.0]])]});
            var Q1;
            Q1=makeQuery(id+"F1.imprint","IMPRINT",FACE,{"disambiguationData":[TD([[makeQuery(id+"F1.imprint","IMPRINT",EDGE,{"derivedFrom":sQuery(id+"F1.wireOp",EDGE,"E174")}),1.0]])]});
            var Q2;
            Q2=makeQuery(id+"F1.imprint","IMPRINT",FACE,{"disambiguationData":[TD([[makeQuery(id+"F1.imprint","IMPRINT",EDGE,{"derivedFrom":sQuery(id+"F1.wireOp",EDGE,"E118")}),1.0]])]});
            var Q3;
            Q3=makeQuery(id+"F1.imprint","IMPRINT",FACE,{"disambiguationData":[TD([[makeQuery(id+"F1.imprint","IMPRINT",EDGE,{"derivedFrom":sQuery(id+"F1.wireOp",EDGE,"E226")}),1.0]])]});
            var Q4;
            Q4=makeQuery(id+"F1.imprint","IMPRINT",FACE,{"disambiguationData":[TD([[makeQuery(id+"F1.imprint","IMPRINT",EDGE,{"derivedFrom":sQuery(id+"F1.wireOp",EDGE,"E6")}),1.0]])]});
            var Q5;
            Q5=makeQuery(id+"F1.imprint","IMPRINT",FACE,{"disambiguationData":[TD([[makeQuery(id+"F1.imprint","IMPRINT",EDGE,{"derivedFrom":sQuery(id+"F1.wireOp",EDGE,"E86")}),1.0]])]});
            extrude(context, id + "F2", {"entities" : qUnion([Q0, Q1, Q2, Q3, Q4, Q5]), "depth" : 2.54 * mm, "offsetDistance" : 25.4 * mm});
        }
    });
